# Revit family: WCPan-RimEx-WallHung-57cm-Vitra-NestSeries-5176
name_source: partatom
category: Plumbing Fixtures
revit_build: Autodesk Revit 2017 (Build: 20160225_1515(x64)
units: mm (PartAtom-declared; Revit-internal decimal feet)

## family parameters
Cut with Voids When Loaded = No
Host = Face
OmniClass Number = 23.45.05.14.14
OmniClass Title = Sinks/Lavatories
Part Type = Normal
Room Calculation Point = No
Round Connector Dimension = Use Diameter
Shared = Yes

## types (10) — shared parameters
BIMobject category = Sanitary - Toilets
Brand = VitrA
CW Connection = Yes
Color = White
Default Elevation = 410 mm  [stored 1.34514 ft]
Design country = Turkey
HW Connection = No
IFC Classification = Sanitary Terminal
Main Material = Ceramic
Manufacturer = Vitra
Manufacturer name = Vitra
Masterformat 2014 Code = 22 45 26
Masterformat 2014 Description = Sanitary Facilities
Mounting type = Wall Hung
NBS Referans Code = 35-65-90
NBS Referans Description = Toilet Systems
Nominal Depth (mm) = 570 mm  [stored 1.87008 ft]
Nominal Height (mm) = 350 mm  [stored 1.14829 ft]
Nominal Width (mm) = 360 mm  [stored 1.1811 ft]
OmniClass Code = 23-31 19 00
OmniClass Description = Toilets
Primary Material = Chrome
Product certification = https://www.vitraglobal.com
Product family = Nest
Product group = Wall Mounted WC
Secondary Material = White
UNSPSC Description = Sanitary Ware
URL = https://www.vitra.com.tr
Uniclass 1.4 Code = L7216
Uniclass 1.4 Description = Toilets
Uniclass 2.0 Code = SS-35-65-90
Uniclass 2.0 Description = Toilet Systems
Uniclass 2015 Code = Pr_40_20_93
Uniclass 2015 Name = Urinal and WC fittings
Uniformat II Code = D2010
Uniformat II Description = Sanitary Facilities
Vent Connection = No
Warranty Period (Year) = 10 Years
Waste Connection = Yes
Weight Net (kg) = 34.3
Youtube = https://www.youtube.com

## per-type parameters (varying)
| type | Article No. (default) | Description | Model | Product SKU | Product url | Technical description | With Bidet Valve |
| WCPan-RimEx-WallHung-57cm-Vitra-NestSeries-5176B003-0101 | 5176B003-0101 | VitrA Nest Rim-Ex Wall Hung WC Without Bidet Function - 58cm - White | 5176B003-0101 | 5176B003-0101 | https://www.vitraglobal.com | https://www.vitraglobal.com | No |
| WCPan-RimEx-WallHung-57cm-Vitra-NestSeries-5176B003-1686 | 5176B003-1686 | VitrA Nest Rim-ex Wall Hung WC With Bidet Function White | 5176B003-1686 | 5176B003-1686 | https://www.vitraglobal.com | https://www.vitraglobal.com | Yes |
| WCPan-RimEx-WallHung-57cm-Vitra-NestSeries-5176B003-1684 | 5176B003-1684 | VitrA Nest Rim-Ex Wall Hung WC With Bidet Function 58cm White | 5176B003-1684 | 5176B003-1684 | https://www.vitraglobal.com | https://www.vitraglobal.com | Yes |
| WCPan-RimEx-WallHung-57cm-Vitra-NestSeries-5176B003-1687 | 5176B003-1687 | VitrA Nest Rim-Ex Wall Hung WC With Bidet Function 58cm White | 5176B003-1687 | 5176B003-1687 | https://www.vitraglobal.com | https://www.vitraglobal.com | Yes |
| WCPan-RimEx-WallHung-57cm-Vitra-NestSeries-5176B003-7211 | 5176B003-7211 | VitrA Nest Rim-Ex Wall Hung WC With Bidet Function 58cm White | 5176B003-7211 | 5176B003-7211 | https://www.vitraglobal.com | https://www.vitraglobal.com | Yes |
| WCPan-RimEx-WallHung-57cm-Vitra-NestSeries-5176B003-7212 | 5176B003-7212 | VitrA Nest Rim-Ex Wall Hung WC With Bidet Function 58cm White | 5176B003-7212 | 5176B003-7212 | https://www.vitraglobal.com | https://www.vitraglobal.com | Yes |
| WCPan-RimEx-WallHung-57cm-Vitra-NestSeries-5176B003H1686 | 5176B003H1686 | VitrA Nest Rim-ex Wall Hung WC With Bidet Function White | 5176B003H1686 | 5176B003H1686 | https://www.vitra-india.com | https://www.vitra-india.com | Yes |
| WCPan-RimEx-WallHung-57cm-Vitra-NestSeries-5176B003H0559 | 5176B003H0559 | VitrA Nest Rim-ex Wall Hung WC With Bidet Function 58cm White | 5176B003H0559 | 5176B003H0559 | https://www.vitra-india.com | https://www.vitra-india.com | Yes |
| WCPan-RimEx-WallHung-57cm-Vitra-NestSeries-5176B003H1687 | 5176B003H1687 | VitrA Nest Rim-Ex Wall Hung WC With Bidet Function 58cm White | 5176B003H1687 | 5176B003H1687 | https://www.vitra-india.com | https://www.vitra-india.com | Yes |
| WCPan-RimEx-WallHung-57cm-Vitra-NestSeries-5176B003H0101 | 5176B003H0101 | VitrA Nest Rim-Ex Wall Hung WC Without Bidet Function - 58cm - White | 5176B003H0101 | 5176B003H0101 | https://www.vitra-india.com | https://www.vitra-india.com | No |

note: [stored X ft] marks values corroborated as IEEE doubles in the binary element streams (Revit-internal decimal feet)

## geometry (parser evidence)
native form markers: Sweep x2
no freeform markers — native parametric forms only
